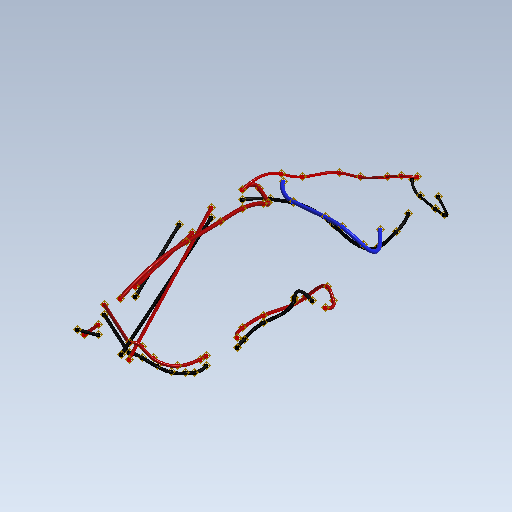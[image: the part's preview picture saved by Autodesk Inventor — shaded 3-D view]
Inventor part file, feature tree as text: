
AUTODESK INVENTOR PART (.ipt)
format: ipt  version: 2020.1 (Build 241239000, 239)  size: 1,635,840 bytes
history: native  units: mm (DEFAULTED — no unit token found)
features: other x137, plane x35, sketch x35, sweep x35
ambient origin geometry x8: Origin, YZ Plane, XZ Plane, XY Plane, X Axis, Y Axis, Z Axis, Center Point
bodies: Body1 (feature_tree), Body2 (feature_tree), Body3 (feature_tree), Body4 (feature_tree), Body5 (feature_tree), Body6 (feature_tree), Body7 (feature_tree), Body8 (feature_tree), Body9 (feature_tree), Body10 (feature_tree), Body11 (feature_tree), Body12 (feature_tree), Body13 (feature_tree), Body14 (feature_tree), Body15 (feature_tree), Body16 (feature_tree), Body17 (feature_tree), Body18 (feature_tree), Body19 (feature_tree), Body20 (feature_tree), Body21 (feature_tree), Body22 (feature_tree), Body23 (feature_tree), Body24 (feature_tree), Body25 (feature_tree), Body26 (feature_tree), Body27 (feature_tree), Body28 (feature_tree), Body29 (feature_tree), Body30 (feature_tree), Body31 (feature_tree), Body32 (feature_tree), Body33 (feature_tree), Body34 (feature_tree), Body35 (feature_tree)
feature tree (242):
  other  "Work Point1"
  other  "Work Point2"
  other  "P- / Switch>XT60"
  other  "Work Point3"
  other  "Work Point4"
  other  "P+ / Switch>XT60"
  other  "Work Point5"
  other  "Work Point6"
  other  "P- / XT60>XT60 VESC1"
  other  "Work Point7"
  other  "Work Point8"
  other  "P+ / XT60>XT60 VESC1"
  other  "Work Point9"
  other  "Work Point10"
  other  "P- / XT60>XT60 VESC2"
  other  "Work Point11"
  other  "Work Point12"
  other  "P+ / XT60>XT60 VESC2"
  other  "Work Point13"
  other  "Work Point14"
  other  "P- / XT60 VESC1>VESC1"
  other  "Work Point15"
  other  "Work Point16"
  other  "P+ / XT60 VESC1>VESC1"
  other  "Work Point17"
  other  "Work Point18"
  other  "P- / XT60 VESC2>VESC2"
  other  "Work Point19"
  other  "Work Point20"
  other  "P+ / XT60 VESC2>VESC2"
  other  "Work Point21"
  other  "Work Point22"
  other  "P- / XT60 B>Switch"
  other  "Work Point23"
  other  "Work Point24"
  other  "P+ / XT60 B>Switch"
  other  "Work Point25"
  other  "Work Point26"
  other  "B- / BAT>BMS"
  other  "Work Point27"
  other  "Work Point28"
  other  "B- / BMS>XT60 B"
  other  "Work Point29"
  other  "Work Point30"
  other  "B+ / BAT>XT60 B"
  other  "Work Point31"
  other  "Work Point32"
  other  "C- / XLR F>BMS"
  other  "Work Point33"
  other  "Work Point34"
  other  "C+ / XLR F>XT60 B"
  plane  "Work Plane9"
  plane  "Work Plane10"
  plane  "Work Plane11"
  plane  "Work Plane12"
  plane  "Work Plane43"
  plane  "Work Plane44"
  plane  "Work Plane47"
  other  "Work Point55"
  other  "Work Point56"
  other  "Segment1"
  other  "Work Point57"
  other  "Work Point58"
  other  "Work Point62"
  other  "Work Point63"
  other  "Segment2"
  other  "Work Point64"
  other  "Work Point65"
  other  "Work Point66"
  plane  "Work Plane54"
  plane  "Work Plane55"
  plane  "Work Plane56"
  other  "Work Point67"
  other  "Work Point68"
  other  "Segment3"
  other  "Work Point69"
  other  "Work Point70"
  plane  "Work Plane57"
  plane  "Work Plane58"
  plane  "Work Plane59"
  other  "Work Point71"
  other  "Work Point72"
  other  "Segment4"
  other  "Work Point73"
  other  "Work Point74"
  other  "Work Point75"
  plane  "Work Plane62"
  plane  "Work Plane64"
  plane  "Work Plane65"
  other  "Work Point77"
  other  "Work Point78"
  other  "Segment5"
  other  "Work Point79"
  plane  "Work Plane66"
  plane  "Work Plane67"
  plane  "Work Plane68"
  other  "Work Point80"
  other  "Work Point81"
  other  "Segment6"
  other  "Work Point82"
  other  "Work Point83"
  other  "Work Point84"
  other  "Work Point85"
  plane  "Work Plane69"
  plane  "Work Plane70"
  plane  "Work Plane71"
  other  "Segment8"
  other  "Work Point95"
  other  "Work Point96"
  other  "Work Point97"
  other  "Work Point98"
  other  "Work Point99"
  other  "Work Point100"
  other  "Work Point101"
  other  "Work Point102"
  other  "Segment9"
  other  "Work Point103"
  other  "Work Point104"
  plane  "Work Plane79"
  plane  "Work Plane80"
  plane  "Work Plane81"
  other  "Work Point105"
  other  "Work Point106"
  other  "Segment10"
  other  "Work Point107"
  other  "Work Point108"
  other  "Work Point109"
  plane  "Work Plane82"
  plane  "Work Plane83"
  plane  "Work Plane84"
  plane  "Work Plane90"
  plane  "Work Plane91"
  plane  "Work Plane92"
  plane  "Work Plane93"
  plane  "Work Plane102"
  plane  "Work Plane103"
  plane  "Work Plane104"
  sketch  "Sketch9"  dims[d16=0.0mm d17=0.0mm d18=0.0mm d19=0.0mm]
  other  "Srf9"
  sketch  "Sketch10"  dims[d20=0.0mm d21=0.0mm d22=0.0mm d23=0.0mm]
  other  "Srf10"
  sketch  "Sketch11"  dims[d76=0.0mm d77=0.0mm d78=0.0mm d79=0.0mm]
  other  "Srf11"
  sketch  "Sketch12"  dims[d84=0.0mm d85=0.0mm d98=0.0mm d99=0.0mm]
  other  "Srf12"
  sketch  "Sketch43"  dims[d100=0.0mm d101=0.0mm d102=0.0mm d103=0.0mm]
  other  "Srf39"
  sketch  "Sketch44"  dims[d104=0.0mm d105=0.0mm d106=0.0mm d107=0.0mm]
  other  "Srf40"
  sketch  "Sketch47"  dims[d108=0.0mm d109=0.0mm d114=0.0mm d115=0.0mm]
  other  "Srf43"
  sketch  "Sketch54"  dims[d118=0.0mm d119=0.0mm d120=0.0mm d121=0.0mm]
  other  "Srf50"
  sketch  "Sketch55"  dims[d122=0.0mm d123=0.0mm d124=0.0mm d125=0.0mm]
  other  "Srf51"
  sketch  "Sketch56"  dims[d126=0.0mm d127=0.0mm d128=0.0mm d129=0.0mm]
  other  "Srf52"
  sketch  "Sketch57"  dims[d130=0.0mm d131=0.0mm d132=0.0mm d133=0.0mm]
  other  "Srf53"
  sketch  "Sketch58"  dims[d148=0.0mm d149=0.0mm d150=0.0mm d151=0.0mm]
  other  "Srf54"
  sketch  "Sketch59"  dims[d152=0.0mm d153=0.0mm d154=0.0mm d155=0.0mm]
  other  "Srf55"
  sketch  "Sketch62"  dims[d156=0.0mm d157=0.0mm d158=0.0mm d159=0.0mm]
  other  "Srf58"
  sketch  "Sketch64"  dims[d168=0.0mm d169=0.0mm d170=0.0mm d171=0.0mm]
  other  "Srf60"
  sketch  "Sketch65"  dims[d172=0.0mm d173=0.0mm d174=0.0mm d175=0.0mm]
  other  "Srf61"
  sketch  "Sketch66"  dims[d190=0.0mm d191=0.0mm d192=0.0mm d193=0.0mm]
  other  "Srf62"
  sketch  "Sketch67"  dims[d194=0.0mm d195=0.0mm]
  other  "Srf63"
  sketch  "Sketch68"
  other  "Srf64"
  sketch  "Sketch69"
  other  "Srf65"
  sketch  "Sketch70"
  other  "Srf66"
  sketch  "Sketch71"
  other  "Srf67"
  sketch  "Sketch79"
  other  "Srf75"
  sketch  "Sketch80"
  other  "Srf76"
  sketch  "Sketch81"
  other  "Srf77"
  sketch  "Sketch82"
  other  "Srf78"
  sketch  "Sketch83"
  other  "Srf79"
  sketch  "Sketch84"
  other  "Srf80"
  sketch  "Sketch90"
  other  "Srf85"
  sketch  "Sketch91"
  other  "Srf86"
  sketch  "Sketch92"
  other  "Srf87"
  sketch  "Sketch93"
  other  "Srf88"
  sketch  "Sketch102"
  other  "Srf96"
  sketch  "Sketch103"
  other  "Srf97"
  sketch  "Sketch104"
  other  "Srf98"
  sweep  "SweepSrf9"
  sweep  "SweepSrf10"
  sweep  "SweepSrf11"
  sweep  "SweepSrf12"
  sweep  "SweepSrf39"
  sweep  "SweepSrf40"
  sweep  "SweepSrf43"
  sweep  "SweepSrf50"
  sweep  "SweepSrf51"
  sweep  "SweepSrf52"
  sweep  "SweepSrf53"
  sweep  "SweepSrf54"
  sweep  "SweepSrf55"
  sweep  "SweepSrf58"
  sweep  "SweepSrf60"
  sweep  "SweepSrf61"
  sweep  "SweepSrf62"
  sweep  "SweepSrf63"
  sweep  "SweepSrf64"
  sweep  "SweepSrf65"
  sweep  "SweepSrf66"
  sweep  "SweepSrf67"
  sweep  "SweepSrf75"
  sweep  "SweepSrf76"
  sweep  "SweepSrf77"
  sweep  "SweepSrf78"
  sweep  "SweepSrf79"
  sweep  "SweepSrf80"
  sweep  "SweepSrf85"
  sweep  "SweepSrf86"
  sweep  "SweepSrf87"
  sweep  "SweepSrf88"
  sweep  "SweepSrf96"
  sweep  "SweepSrf97"
  sweep  "SweepSrf98"
